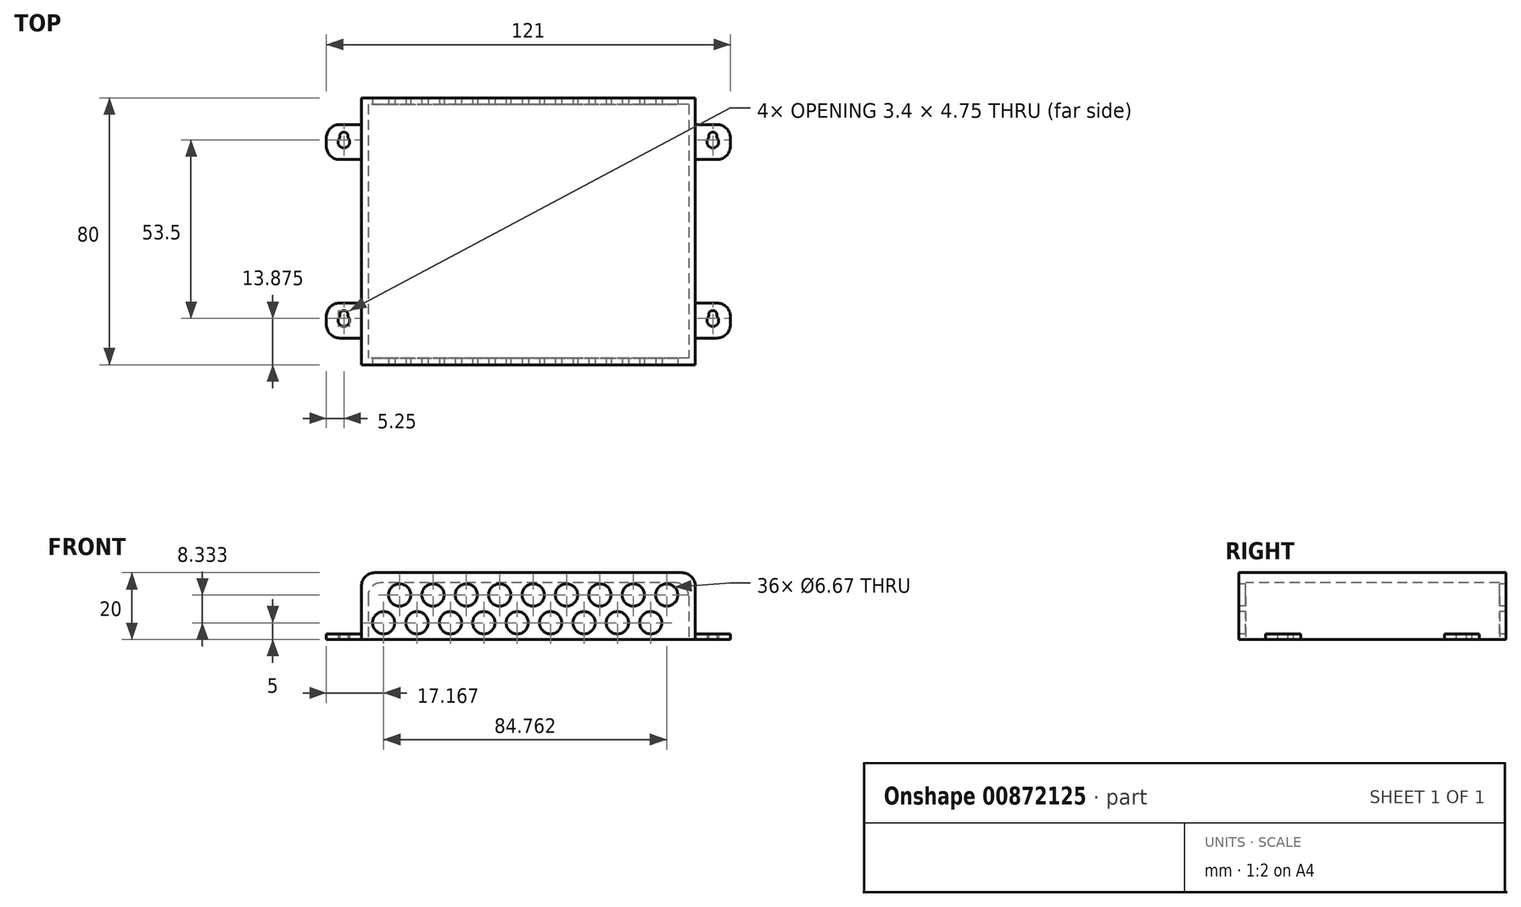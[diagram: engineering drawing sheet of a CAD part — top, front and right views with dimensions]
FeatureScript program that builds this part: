
annotation { "Feature Type Name" : "Feature", "Feature Type Description" : "" }
export const myFeature = defineFeature(function(context is Context, id is Id, definition is map)
    precondition{}
    {
        {
            assignVariable(context, id + "F0", {"name" : "d", "anyValue" : 20});
        }
        {
            var Q0;
            Q0=qCreatedBy(makeId("Top.planeOp"),FACE);
            var sketch = newSketch(context, id + "F1", { "sketchPlane" : qUnion([Q0])});
            skLineSegment(sketch, "E0.bottom", {"start": v(0, 40) * mm, "end": v(50, 40) * mm});
            skLineSegment(sketch, "E0.top", {"start": v(0, -40) * mm, "end": v(50, -40) * mm});
            skLineSegment(sketch, "E0.left", {"start": v(0, 40) * mm, "end": v(0, -40) * mm});
            skLineSegment(sketch, "E0.right", {"start": v(50, 40) * mm, "end": v(50, -40) * mm});
            skLineSegment(sketch, "E1.bottom", {"start": v(50, -21.5) * mm, "end": v(60.5, -21.5) * mm});
            skLineSegment(sketch, "E1.top", {"start": v(50, -32) * mm, "end": v(60.5, -32) * mm});
            skLineSegment(sketch, "E1.left", {"start": v(50, -21.5) * mm, "end": v(50, -32) * mm});
            skLineSegment(sketch, "E1.right", {"start": v(60.5, -21.5) * mm, "end": v(60.5, -32) * mm});
            skCircle(sketch, "E2", {"center": v(55.25, -26.75) * mm, "radius": 1.75 * mm});
            skLineSegment(sketch, "E3", {"start": v(55.25, -21.5) * mm, "end": v(55.25, -32) * mm, "construction": true});
            skLineSegment(sketch, "E4", {"start": v(60.5, -26.75) * mm, "end": v(50, -26.75) * mm, "construction": true});
            skLineSegment(sketch, "E5.bottom", {"start": v(50, 32) * mm, "end": v(60.5, 32) * mm});
            skLineSegment(sketch, "E5.top", {"start": v(50, 21.5) * mm, "end": v(60.5, 21.5) * mm});
            skLineSegment(sketch, "E5.left", {"start": v(50, 32) * mm, "end": v(50, 21.5) * mm});
            skLineSegment(sketch, "E5.right", {"start": v(60.5, 32) * mm, "end": v(60.5, 21.5) * mm});
            skCircle(sketch, "E6", {"center": v(55.25, 26.75) * mm, "radius": 1.75 * mm});
            skLineSegment(sketch, "E7", {"start": v(55.25, 32) * mm, "end": v(55.25, 21.5) * mm, "construction": true});
            skLineSegment(sketch, "E8", {"start": v(60.5, 26.75) * mm, "end": v(50, 26.75) * mm, "construction": true});
            skCircle(sketch, "E9", {"center": v(55.25, -25) * mm, "radius": 1.25 * mm});
            skCircle(sketch, "E10", {"center": v(55.25, 28.5) * mm, "radius": 1.25 * mm});
            skCircle(sketch, "E11.MirrorC", {"center": v(-55.25, -25) * mm, "radius": 1.25 * mm});
            skCircle(sketch, "E12.MirrorC", {"center": v(-55.25, 28.5) * mm, "radius": 1.25 * mm});
            skLineSegment(sketch, "E13.MirrorCS", {"start": v(-50, 32) * mm, "end": v(-50, 21.5) * mm});
            skLineSegment(sketch, "E14.MirrorCS", {"start": v(-50, 21.5) * mm, "end": v(-60.5, 21.5) * mm});
            skCircle(sketch, "E15.MirrorC", {"center": v(-55.25, -26.75) * mm, "radius": 1.75 * mm});
            skLineSegment(sketch, "E16.MirrorCS", {"start": v(-55.25, 32) * mm, "end": v(-55.25, 21.5) * mm, "construction": true});
            skLineSegment(sketch, "E17.MirrorCS", {"start": v(-50, 32) * mm, "end": v(-60.5, 32) * mm});
            skLineSegment(sketch, "E18.MirrorCS", {"start": v(-60.5, 32) * mm, "end": v(-60.5, 21.5) * mm});
            skCircle(sketch, "E19.MirrorC", {"center": v(-55.25, 26.75) * mm, "radius": 1.75 * mm});
            skLineSegment(sketch, "E20.MirrorCS", {"start": v(-60.5, -26.75) * mm, "end": v(-50, -26.75) * mm, "construction": true});
            skLineSegment(sketch, "E21.MirrorCS", {"start": v(-55.25, -21.5) * mm, "end": v(-55.25, -32) * mm, "construction": true});
            skLineSegment(sketch, "E22.MirrorCS", {"start": v(-60.5, 26.75) * mm, "end": v(-50, 26.75) * mm, "construction": true});
            skLineSegment(sketch, "E23.MirrorCS", {"start": v(-60.5, -21.5) * mm, "end": v(-60.5, -32) * mm});
            skLineSegment(sketch, "E24.MirrorCS", {"start": v(-50, -21.5) * mm, "end": v(-50, -32) * mm});
            skLineSegment(sketch, "E25.MirrorCS", {"start": v(-50, -32) * mm, "end": v(-60.5, -32) * mm});
            skLineSegment(sketch, "E26.MirrorCS", {"start": v(-50, -21.5) * mm, "end": v(-60.5, -21.5) * mm});
            skLineSegment(sketch, "E27.MirrorCS", {"start": v(-50, 40) * mm, "end": v(-50, -40) * mm});
            skLineSegment(sketch, "E28.MirrorCS", {"start": v(0, -40) * mm, "end": v(-50, -40) * mm});
            skLineSegment(sketch, "E29.MirrorCS", {"start": v(0, 40) * mm, "end": v(-50, 40) * mm});
            skLineSegment(sketch, "E30.0", {"start": v(0, -38) * mm, "end": v(48, -38) * mm});
            skLineSegment(sketch, "E30.1", {"start": v(-48, 38) * mm, "end": v(-48, -38) * mm});
            skLineSegment(sketch, "E30.2", {"start": v(0, 38) * mm, "end": v(-48, 38) * mm});
            skLineSegment(sketch, "E30.3", {"start": v(0, -38) * mm, "end": v(-48, -38) * mm});
            skLineSegment(sketch, "E30.4", {"start": v(0, 38) * mm, "end": v(48, 38) * mm});
            skLineSegment(sketch, "E30.5", {"start": v(48, 38) * mm, "end": v(48, -38) * mm});
            skSolve(sketch);
        }
        {
            var Q0;
            Q0=makeQuery(id+"F1.imprint","IMPRINT",FACE,{"disambiguationData":[TD([[makeQuery(id+"F1.imprint","IMPRINT",EDGE,{"derivedFrom":sQuery(id+"F1.wireOp",EDGE,"E0.left")}),-1.0]])]});
            var Q1;
            {var subQ3=sQuery(id+"F1.wireOp",EDGE,"E0.bottom");Q1=makeQuery(id+"F1.imprint","IMPRINT",FACE,{"disambiguationData":[TD([[makeQuery(id+"F1.imprint","IMPRINT",EDGE,{"derivedFrom":subQ3}),-1.0]])]});}
            var Q2;
            Q2=makeQuery(id+"F1.imprint","IMPRINT",FACE,{"disambiguationData":[TD([[makeQuery(id+"F1.imprint","IMPRINT",EDGE,{"derivedFrom":sQuery(id+"F1.wireOp",EDGE,"E30.1")}),1.0]])]});
            var Q3;
            {var subQ0=sQuery(id+"F1.wireOp",EDGE,"E30.0");Q3=makeQuery(id+"F1.imprint","IMPRINT",FACE,{"disambiguationData":[TD([[makeQuery(id+"F1.imprint","IMPRINT",EDGE,{"derivedFrom":subQ0}),1.0]])]});}
            extrude(context, id + "F2", {"entities" : qUnion([Q0, Q1, Q2, Q3]), "depth" : (getVariable(context, 'd')) * mm, "offsetDistance" : 25 * mm});
        }
        {
            var Q0;
            Q0=makeQuery(id+"F1.imprint","IMPRINT",FACE,{"disambiguationData":[TD([[makeQuery(id+"F1.imprint","IMPRINT",EDGE,{"derivedFrom":sQuery(id+"F1.wireOp",EDGE,"E30.1")}),1.0]])]});
            var Q1;
            {var subQ0=sQuery(id+"F1.wireOp",EDGE,"E30.0");Q1=makeQuery(id+"F1.imprint","IMPRINT",FACE,{"disambiguationData":[TD([[makeQuery(id+"F1.imprint","IMPRINT",EDGE,{"derivedFrom":subQ0}),1.0]])]});}
            extrude(context, id + "F3", {"entities" : qUnion([Q0, Q1]), "operationType" : NewBodyOperationType.REMOVE, "depth" : 17 * mm, "offsetDistance" : 25 * mm});
        }
        {
            var Q0;
            Q0=makeQuery(id+"F1.imprint","IMPRINT",FACE,{"disambiguationData":[TD([[makeQuery(id+"F1.imprint","IMPRINT",EDGE,{"derivedFrom":sQuery(id+"F1.wireOp",EDGE,"E23.MirrorCS")}),1.0]])]});
            var Q1;
            {var subQ1=sQuery(id+"F1.wireOp",EDGE,"E14.MirrorCS");Q1=makeQuery(id+"F1.imprint","IMPRINT",FACE,{"disambiguationData":[TD([[makeQuery(id+"F1.imprint","IMPRINT",EDGE,{"derivedFrom":subQ1}),-1.0]])]});}
            var Q2;
            Q2=makeQuery(id+"F1.imprint","IMPRINT",FACE,{"disambiguationData":[TD([[makeQuery(id+"F1.imprint","IMPRINT",EDGE,{"derivedFrom":sQuery(id+"F1.wireOp",EDGE,"E5.bottom")}),-1.0]])]});
            var Q3;
            Q3=makeQuery(id+"F1.imprint","IMPRINT",FACE,{"disambiguationData":[TD([[makeQuery(id+"F1.imprint","IMPRINT",EDGE,{"derivedFrom":sQuery(id+"F1.wireOp",EDGE,"E1.bottom")}),-1.0]])]});
            extrude(context, id + "F4", {"entities" : qUnion([Q0, Q1, Q2, Q3]), "operationType" : NewBodyOperationType.ADD, "depth" : 1.7 * mm, "offsetDistance" : 25 * mm});
        }
        {
            var Q0;
            Q0=makeQuery(id+"F2.opExtrude","SWEPT_FACE",FACE,{"disambiguationData":[OSD([sQuery(id+"F1.wireOp",EDGE,"E0.top"),sQuery(id+"F1.wireOp",EDGE,"E28.MirrorCS")])]});
            var sketch = newSketch(context, id + "F5", { "sketchPlane" : qUnion([Q0])});
            skLineSegment(sketch, "E31", {"start": v(-50, 10) * mm, "end": v(50, 10) * mm, "construction": true});
            skLineSegment(sketch, "E32.0.0", {"start": v(-50, 0) * mm, "end": v(50, 0) * mm});
            skLineSegment(sketch, "E32.0.1", {"start": v(50, 0) * mm, "end": v(50, 10) * mm});
            skLineSegment(sketch, "E32.0.2", {"start": v(50, 20) * mm, "end": v(-50, 20) * mm});
            skLineSegment(sketch, "E32.0.3", {"start": v(-50, 20) * mm, "end": v(-50, 10) * mm});
            skLineSegment(sketch, "E33", {"start": v(-50, 10) * mm, "end": v(-50, 0) * mm});
            skLineSegment(sketch, "E34", {"start": v(50, 10) * mm, "end": v(50, 20) * mm});
            skLineSegment(sketch, "E35", {"start": v(50, 13.33) * mm, "end": v(-50, 13.33) * mm, "construction": true});
            skLineSegment(sketch, "E36", {"start": v(-50, 5) * mm, "end": v(50, 5) * mm, "construction": true});
            skCircle(sketch, "E37", {"center": v(-43.33, 5) * mm, "radius": 3.33 * mm});
            skCircle(sketch, "E38.1.0.0", {"center": v(-33.33, 5) * mm, "radius": 3.33 * mm});
            skCircle(sketch, "E38.2.0.0", {"center": v(-23.33, 5) * mm, "radius": 3.33 * mm});
            skCircle(sketch, "E38.3.0.0", {"center": v(-13.33, 5) * mm, "radius": 3.33 * mm});
            skCircle(sketch, "E38.4.0.0", {"center": v(-3.33, 5) * mm, "radius": 3.33 * mm});
            skCircle(sketch, "E38.5.0.0", {"center": v(6.67, 5) * mm, "radius": 3.33 * mm});
            skCircle(sketch, "E38.6.0.0", {"center": v(16.67, 5) * mm, "radius": 3.33 * mm});
            skCircle(sketch, "E38.7.0.0", {"center": v(26.67, 5) * mm, "radius": 3.33 * mm});
            skCircle(sketch, "E38.8.0.0", {"center": v(36.67, 5) * mm, "radius": 3.33 * mm});
            skLineSegment(sketch, "E38.direction1", {"start": v(-43.33, 5) * mm, "end": v(-33.33, 5) * mm, "construction": true});
            skCircle(sketch, "E39", {"center": v(-38.57, 13.33) * mm, "radius": 3.33 * mm});
            skCircle(sketch, "E40.1.0.0", {"center": v(-28.57, 13.33) * mm, "radius": 3.33 * mm});
            skCircle(sketch, "E40.2.0.0", {"center": v(-18.57, 13.33) * mm, "radius": 3.33 * mm});
            skCircle(sketch, "E40.3.0.0", {"center": v(-8.57, 13.33) * mm, "radius": 3.33 * mm});
            skCircle(sketch, "E40.4.0.0", {"center": v(1.43, 13.33) * mm, "radius": 3.33 * mm});
            skCircle(sketch, "E40.5.0.0", {"center": v(11.43, 13.33) * mm, "radius": 3.33 * mm});
            skCircle(sketch, "E40.6.0.0", {"center": v(21.43, 13.33) * mm, "radius": 3.33 * mm});
            skCircle(sketch, "E40.7.0.0", {"center": v(31.43, 13.33) * mm, "radius": 3.33 * mm});
            skCircle(sketch, "E40.8.0.0", {"center": v(41.43, 13.33) * mm, "radius": 3.33 * mm});
            skLineSegment(sketch, "E40.direction1", {"start": v(-38.57, 13.33) * mm, "end": v(-28.57, 13.33) * mm, "construction": true});
            skSolve(sketch);
        }
        {
            var Q0;
            Q0=makeQuery(id+"F5.imprint","IMPRINT",FACE,{"disambiguationData":[TD([[makeQuery(id+"F5.imprint","IMPRINT",EDGE,{"derivedFrom":sQuery(id+"F5.wireOp",EDGE,"E39")}),1.0]])]});
            var Q1;
            Q1=makeQuery(id+"F5.imprint","IMPRINT",FACE,{"disambiguationData":[TD([[makeQuery(id+"F5.imprint","IMPRINT",EDGE,{"derivedFrom":sQuery(id+"F5.wireOp",EDGE,"E37")}),1.0]])]});
            var Q2;
            Q2=makeQuery(id+"F5.imprint","IMPRINT",FACE,{"disambiguationData":[TD([[makeQuery(id+"F5.imprint","IMPRINT",EDGE,{"derivedFrom":sQuery(id+"F5.wireOp",EDGE,"E38.1.0.0")}),1.0]])]});
            var Q3;
            Q3=makeQuery(id+"F5.imprint","IMPRINT",FACE,{"disambiguationData":[TD([[makeQuery(id+"F5.imprint","IMPRINT",EDGE,{"derivedFrom":sQuery(id+"F5.wireOp",EDGE,"E40.1.0.0")}),1.0]])]});
            var Q4;
            Q4=makeQuery(id+"F5.imprint","IMPRINT",FACE,{"disambiguationData":[TD([[makeQuery(id+"F5.imprint","IMPRINT",EDGE,{"derivedFrom":sQuery(id+"F5.wireOp",EDGE,"E38.2.0.0")}),1.0]])]});
            var Q5;
            Q5=makeQuery(id+"F5.imprint","IMPRINT",FACE,{"disambiguationData":[TD([[makeQuery(id+"F5.imprint","IMPRINT",EDGE,{"derivedFrom":sQuery(id+"F5.wireOp",EDGE,"E40.2.0.0")}),1.0]])]});
            var Q6;
            Q6=makeQuery(id+"F5.imprint","IMPRINT",FACE,{"disambiguationData":[TD([[makeQuery(id+"F5.imprint","IMPRINT",EDGE,{"derivedFrom":sQuery(id+"F5.wireOp",EDGE,"E38.3.0.0")}),1.0]])]});
            var Q7;
            Q7=makeQuery(id+"F5.imprint","IMPRINT",FACE,{"disambiguationData":[TD([[makeQuery(id+"F5.imprint","IMPRINT",EDGE,{"derivedFrom":sQuery(id+"F5.wireOp",EDGE,"E40.3.0.0")}),1.0]])]});
            var Q8;
            Q8=makeQuery(id+"F5.imprint","IMPRINT",FACE,{"disambiguationData":[TD([[makeQuery(id+"F5.imprint","IMPRINT",EDGE,{"derivedFrom":sQuery(id+"F5.wireOp",EDGE,"E38.4.0.0")}),1.0]])]});
            var Q9;
            Q9=makeQuery(id+"F5.imprint","IMPRINT",FACE,{"disambiguationData":[TD([[makeQuery(id+"F5.imprint","IMPRINT",EDGE,{"derivedFrom":sQuery(id+"F5.wireOp",EDGE,"E40.4.0.0")}),1.0]])]});
            var Q10;
            Q10=makeQuery(id+"F5.imprint","IMPRINT",FACE,{"disambiguationData":[TD([[makeQuery(id+"F5.imprint","IMPRINT",EDGE,{"derivedFrom":sQuery(id+"F5.wireOp",EDGE,"E38.5.0.0")}),1.0]])]});
            var Q11;
            Q11=makeQuery(id+"F5.imprint","IMPRINT",FACE,{"disambiguationData":[TD([[makeQuery(id+"F5.imprint","IMPRINT",EDGE,{"derivedFrom":sQuery(id+"F5.wireOp",EDGE,"E40.5.0.0")}),1.0]])]});
            var Q12;
            Q12=makeQuery(id+"F5.imprint","IMPRINT",FACE,{"disambiguationData":[TD([[makeQuery(id+"F5.imprint","IMPRINT",EDGE,{"derivedFrom":sQuery(id+"F5.wireOp",EDGE,"E38.6.0.0")}),1.0]])]});
            var Q13;
            Q13=makeQuery(id+"F5.imprint","IMPRINT",FACE,{"disambiguationData":[TD([[makeQuery(id+"F5.imprint","IMPRINT",EDGE,{"derivedFrom":sQuery(id+"F5.wireOp",EDGE,"E40.6.0.0")}),1.0]])]});
            var Q14;
            Q14=makeQuery(id+"F5.imprint","IMPRINT",FACE,{"disambiguationData":[TD([[makeQuery(id+"F5.imprint","IMPRINT",EDGE,{"derivedFrom":sQuery(id+"F5.wireOp",EDGE,"E38.7.0.0")}),1.0]])]});
            var Q15;
            Q15=makeQuery(id+"F5.imprint","IMPRINT",FACE,{"disambiguationData":[TD([[makeQuery(id+"F5.imprint","IMPRINT",EDGE,{"derivedFrom":sQuery(id+"F5.wireOp",EDGE,"E40.7.0.0")}),1.0]])]});
            var Q16;
            Q16=makeQuery(id+"F5.imprint","IMPRINT",FACE,{"disambiguationData":[TD([[makeQuery(id+"F5.imprint","IMPRINT",EDGE,{"derivedFrom":sQuery(id+"F5.wireOp",EDGE,"E40.8.0.0")}),1.0]])]});
            var Q17;
            Q17=makeQuery(id+"F5.imprint","IMPRINT",FACE,{"disambiguationData":[TD([[makeQuery(id+"F5.imprint","IMPRINT",EDGE,{"derivedFrom":sQuery(id+"F5.wireOp",EDGE,"E38.8.0.0")}),1.0]])]});
            var Q18;
            Q18=makeQuery(id+"F5.imprint","IMPRINT",FACE,{"disambiguationData":[TD([[makeQuery(id+"F5.imprint","IMPRINT",EDGE,{"derivedFrom":sQuery(id+"F5.wireOp",EDGE,"E38.9.0.0")}),1.0]])]});
            var Q19;
            Q19=makeQuery(id+"F3.boolean.opBoolean","COPY",FACE,{"derivedFrom":makeQuery(id+"F3.opExtrude","SWEPT_FACE",FACE,{"disambiguationData":[OSD([sQuery(id+"F1.wireOp",EDGE,"E30.0"),sQuery(id+"F1.wireOp",EDGE,"E30.3")])]})});
            extrude(context, id + "F6", {"entities" : qUnion([Q0, Q1, Q2, Q3, Q4, Q5, Q6, Q7, Q8, Q9, Q10, Q11, Q12, Q13, Q14, Q15, Q16, Q17, Q18]), "operationType" : NewBodyOperationType.REMOVE, "endBound" : BoundingType.THROUGH_ALL, "oppositeDirection" : true, "depth" : 25 * mm, "endBoundEntityFace" : qUnion([Q19]), "offsetDistance" : 25 * mm});
        }
        {
            var Q0;
            Q0=makeQuery(id+"F4.opExtrude","SWEPT_EDGE",EDGE,{"disambiguationData":[OSD([sQuery(id+"F1.wireOp",EDGE,"E17.MirrorCS"),sQuery(id+"F1.wireOp",EDGE,"E18.MirrorCS")])]});
            var Q1;
            Q1=makeQuery(id+"F4.opExtrude","SWEPT_EDGE",EDGE,{"disambiguationData":[OSD([sQuery(id+"F1.wireOp",EDGE,"E14.MirrorCS"),sQuery(id+"F1.wireOp",EDGE,"E18.MirrorCS")])]});
            var Q2;
            Q2=makeQuery(id+"F4.opExtrude","SWEPT_EDGE",EDGE,{"disambiguationData":[OSD([sQuery(id+"F1.wireOp",EDGE,"E14.MirrorCS"),sQuery(id+"F1.wireOp",EDGE,"E27.MirrorCS")])]});
            var Q3;
            Q3=makeQuery(id+"F4.opExtrude","SWEPT_EDGE",EDGE,{"disambiguationData":[OSD([sQuery(id+"F1.wireOp",EDGE,"E25.MirrorCS"),sQuery(id+"F1.wireOp",EDGE,"E27.MirrorCS")])]});
            var Q4;
            Q4=makeQuery(id+"F4.opExtrude","SWEPT_EDGE",EDGE,{"disambiguationData":[OSD([sQuery(id+"F1.wireOp",EDGE,"E23.MirrorCS"),sQuery(id+"F1.wireOp",EDGE,"E25.MirrorCS")])]});
            var Q5;
            Q5=makeQuery(id+"F4.opExtrude","SWEPT_EDGE",EDGE,{"disambiguationData":[OSD([sQuery(id+"F1.wireOp",EDGE,"E23.MirrorCS"),sQuery(id+"F1.wireOp",EDGE,"E26.MirrorCS")])]});
            var Q6;
            Q6=makeQuery(id+"F4.opExtrude","SWEPT_EDGE",EDGE,{"disambiguationData":[OSD([sQuery(id+"F1.wireOp",EDGE,"E17.MirrorCS"),sQuery(id+"F1.wireOp",EDGE,"E27.MirrorCS")])]});
            var Q7;
            Q7=makeQuery(id+"F4.opExtrude","SWEPT_EDGE",EDGE,{"disambiguationData":[OSD([sQuery(id+"F1.wireOp",EDGE,"E26.MirrorCS"),sQuery(id+"F1.wireOp",EDGE,"E27.MirrorCS")])]});
            var Q8;
            {var subQ0=sQuery(id+"F1.wireOp",EDGE,"E27.MirrorCS");Q8=makeQuery(id+"F4.opExtrude","CAP_EDGE",EDGE,{"disambiguationData":[OSD([subQ0]),TDD([makeQuery(id+"F1.imprint","IMPRINT",EDGE,{"disambiguationData":[TD([[makeQuery(id+"F1.imprint","INTERSECT",VERTEX,{"derivedFrom":[sQuery(id+"F1.wireOp",EDGE,"E14.MirrorCS"),subQ0]}),1.0]])],"derivedFrom":subQ0})])],"isStart":false});}
            var Q9;
            {var subQ0=sQuery(id+"F1.wireOp",EDGE,"E27.MirrorCS");Q9=makeQuery(id+"F4.opExtrude","CAP_EDGE",EDGE,{"disambiguationData":[OSD([subQ0]),TDD([makeQuery(id+"F1.imprint","IMPRINT",EDGE,{"disambiguationData":[TD([[makeQuery(id+"F1.imprint","INTERSECT",VERTEX,{"derivedFrom":[sQuery(id+"F1.wireOp",EDGE,"E25.MirrorCS"),subQ0]}),1.0]])],"derivedFrom":subQ0})])],"isStart":false});}
            var Q10;
            Q10=makeQuery(id+"F4.opExtrude","CAP_EDGE",EDGE,{"disambiguationData":[OSD([sQuery(id+"F1.wireOp",EDGE,"E1.left")])],"isStart":false});
            var Q11;
            Q11=makeQuery(id+"F4.opExtrude","CAP_EDGE",EDGE,{"disambiguationData":[OSD([sQuery(id+"F1.wireOp",EDGE,"E5.left")])],"isStart":false});
            var Q12;
            Q12=makeQuery(id+"F4.opExtrude","SWEPT_EDGE",EDGE,{"disambiguationData":[OSD([sQuery(id+"F1.wireOp",EDGE,"E0.right"),sQuery(id+"F1.wireOp",EDGE,"E5.top"),sQuery(id+"F1.wireOp",EDGE,"E5.left")])]});
            var Q13;
            Q13=makeQuery(id+"F4.opExtrude","SWEPT_EDGE",EDGE,{"disambiguationData":[OSD([sQuery(id+"F1.wireOp",EDGE,"E5.top"),sQuery(id+"F1.wireOp",EDGE,"E5.right")])]});
            var Q14;
            Q14=makeQuery(id+"F4.opExtrude","SWEPT_EDGE",EDGE,{"disambiguationData":[OSD([sQuery(id+"F1.wireOp",EDGE,"E5.bottom"),sQuery(id+"F1.wireOp",EDGE,"E5.right")])]});
            var Q15;
            Q15=makeQuery(id+"F4.opExtrude","SWEPT_EDGE",EDGE,{"disambiguationData":[OSD([sQuery(id+"F1.wireOp",EDGE,"E1.bottom"),sQuery(id+"F1.wireOp",EDGE,"E1.right")])]});
            var Q16;
            Q16=makeQuery(id+"F4.opExtrude","SWEPT_EDGE",EDGE,{"disambiguationData":[OSD([sQuery(id+"F1.wireOp",EDGE,"E1.top"),sQuery(id+"F1.wireOp",EDGE,"E1.right")])]});
            var Q17;
            Q17=makeQuery(id+"F4.opExtrude","SWEPT_EDGE",EDGE,{"disambiguationData":[OSD([sQuery(id+"F1.wireOp",EDGE,"E0.right"),sQuery(id+"F1.wireOp",EDGE,"E1.top"),sQuery(id+"F1.wireOp",EDGE,"E1.left")])]});
            var Q18;
            Q18=makeQuery(id+"F4.opExtrude","SWEPT_EDGE",EDGE,{"disambiguationData":[OSD([sQuery(id+"F1.wireOp",EDGE,"E0.right"),sQuery(id+"F1.wireOp",EDGE,"E1.bottom"),sQuery(id+"F1.wireOp",EDGE,"E1.left")])]});
            var Q19;
            Q19=makeQuery(id+"F4.opExtrude","SWEPT_EDGE",EDGE,{"disambiguationData":[OSD([sQuery(id+"F1.wireOp",EDGE,"E0.right"),sQuery(id+"F1.wireOp",EDGE,"E5.bottom"),sQuery(id+"F1.wireOp",EDGE,"E5.left")])]});
            var Q20;
            Q20=makeQuery(id+"F2.opExtrude","CAP_EDGE",EDGE,{"disambiguationData":[OSD([sQuery(id+"F1.wireOp",EDGE,"E0.right"),sQuery(id+"F1.wireOp",EDGE,"E1.left"),sQuery(id+"F1.wireOp",EDGE,"E5.left")])],"isStart":false});
            var Q21;
            Q21=makeQuery(id+"F2.opExtrude","CAP_EDGE",EDGE,{"disambiguationData":[OSD([sQuery(id+"F1.wireOp",EDGE,"E27.MirrorCS")])],"isStart":false});
            var Q22;
            Q22=makeQuery(id+"F3.boolean.opBoolean","COPY",EDGE,{"derivedFrom":makeQuery(id+"F3.opExtrude","CAP_EDGE",EDGE,{"disambiguationData":[OSD([sQuery(id+"F1.wireOp",EDGE,"E30.1")])],"isStart":false})});
            var Q23;
            Q23=makeQuery(id+"F3.boolean.opBoolean","COPY",EDGE,{"derivedFrom":makeQuery(id+"F3.opExtrude","CAP_EDGE",EDGE,{"disambiguationData":[OSD([sQuery(id+"F1.wireOp",EDGE,"E30.5")])],"isStart":false})});
            fillet(context, id + "F7", {"entities" : qUnion([Q0, Q1, Q2, Q3, Q4, Q5, Q6, Q7, Q8, Q9, Q10, Q11, Q12, Q13, Q14, Q15, Q16, Q17, Q18, Q19, Q20, Q21, Q22, Q23]), "radius" : (getVariable(context, 'd') / 5) * mm, "tangentPropagation" : true, "allowEdgeOverflow" : false});
        }
    });
